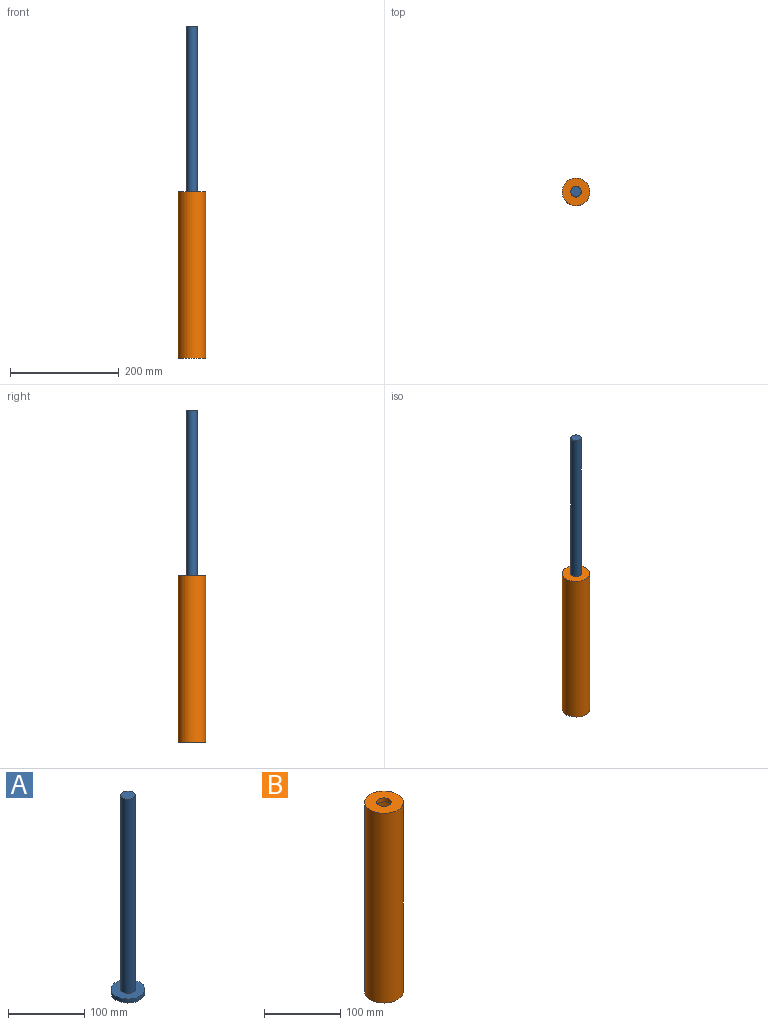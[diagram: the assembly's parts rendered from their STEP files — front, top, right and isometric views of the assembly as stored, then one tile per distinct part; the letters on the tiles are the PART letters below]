
ASSEMBLY  parts=2 mates=4
PART A: 5 faces, bbox 44.5x44.5x317.5 mm
  f0: cylinder r=9.53mm len=311.15mm, axis (0,0,-1), area 18621.5mm2, adj f1,f4
  f1: plane 19.05x19.05mm, normal (0,0,1), area 285mm2, adj f0
  f2: cylinder r=22.23mm len=44.45mm, axis (0,0,1), area 886.7mm2, adj f3,f4
  f3: plane 44.45x44.45mm, normal (0,0,-1), area 1551.8mm2, adj f2
  f4: plane 44.45x44.45mm, normal (0,0,1), area 1266.8mm2, adj f0,f2
PART B: 7 faces, bbox 50.8x50.8x304.8 mm
  f0: cylinder r=25.4mm len=304.8mm, axis (0,0,-1), area 48643.9mm2, adj f1,f2
  f1: plane 50.8x50.8mm, normal (0,0,1), area 1741.8mm2, adj f0,f3
  f2: plane 50.8x50.8mm, normal (0,0,-1), area 2026.8mm2, adj f0
  f3: cylinder r=9.53mm len=19.05mm, axis (0,0,1), area 380mm2, adj f1,f4
  f4: plane 44.45x44.45mm, normal (0,0,-1), area 1266.8mm2, adj f3,f6
  f5: plane 44.45x44.45mm, normal (0,0,1), area 1551.8mm2, adj f6
  f6: cylinder r=22.23mm len=292.1mm, axis (0,0,-1), area 40790mm2, adj f4,f5
PLACE A rot(axis=(0,0,1),90deg) t=(-18.24,-2.36,322.56)mm
PLACE B t=(-18.24,-2.36,24.11)mm
MATE parallel A.f2 <-> B.f6  axis (0,0,-1) through (-18.24,-2.36,316.21)mm
MATE cylindrical A.f0 <-> B.f6  axis (0,0,-1) through (-18.24,-2.36,478.13)mm
MATE slider A.f0 <-> B.f0  axis (0,0,-1) through (-18.24,-2.36,478.13)mm
MATE parallel A.f2 <-> B.f6  axis (0,0,1) through (-18.24,-2.36,322.56)mm
